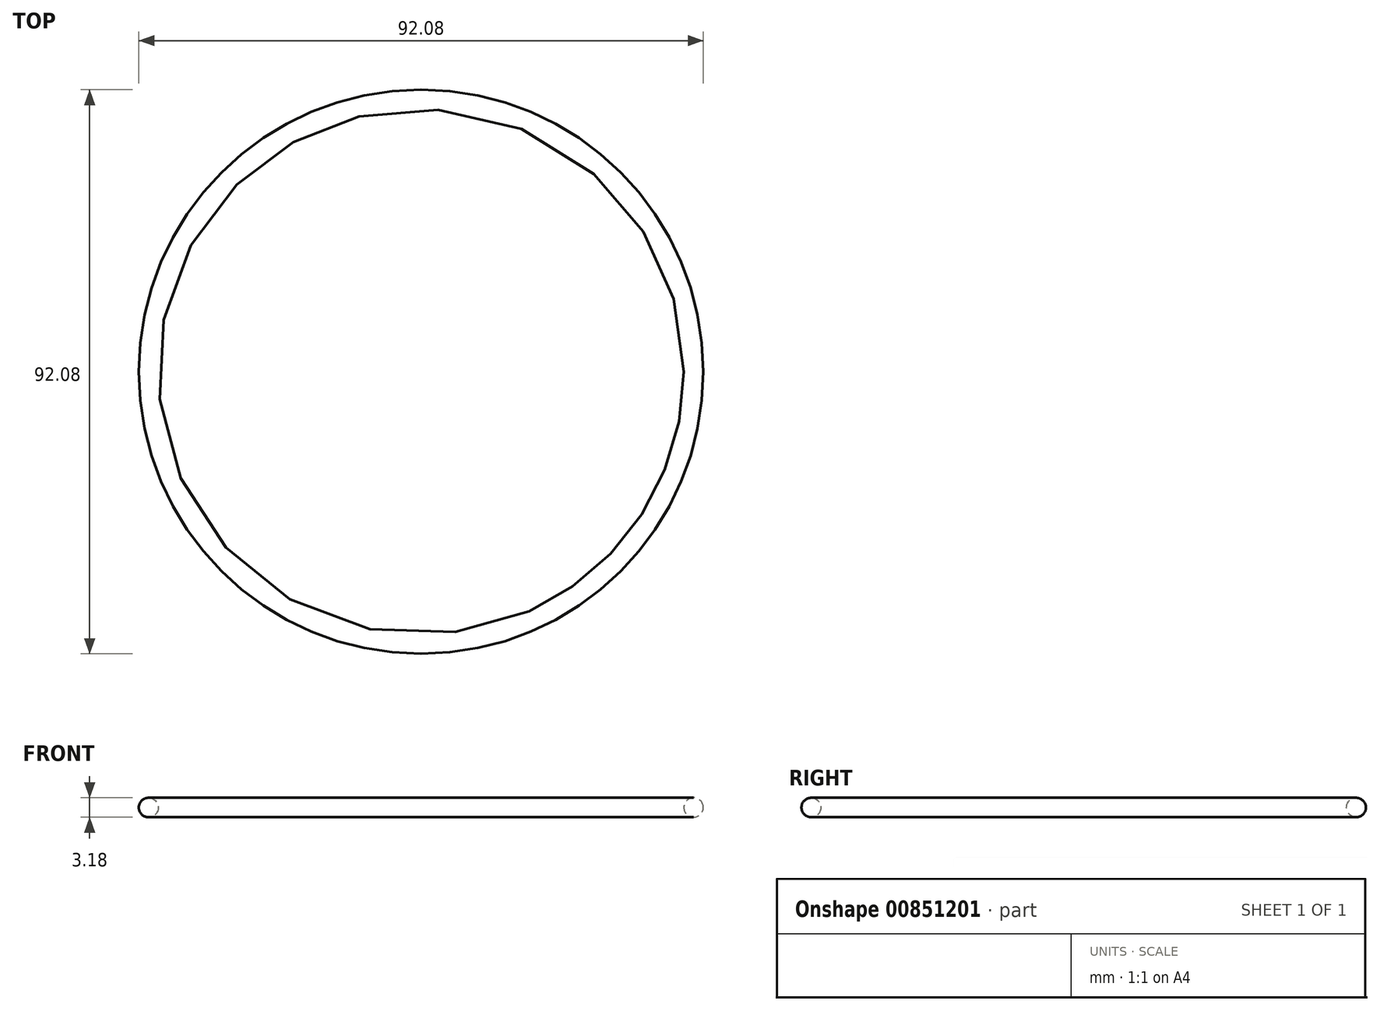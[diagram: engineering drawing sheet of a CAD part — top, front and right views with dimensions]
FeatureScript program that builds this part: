
annotation { "Feature Type Name" : "Feature", "Feature Type Description" : "" }
export const myFeature = defineFeature(function(context is Context, id is Id, definition is map)
    precondition{}
    {
        {
            var Q0;
            Q0=qCreatedBy(makeId("Front.planeOp"),FACE);
            var sketch = newSketch(context, id + "F0", { "sketchPlane" : qUnion([Q0])});
            skCircle(sketch, "E0", {"center": v(44.45, 0) * mm, "radius": 1.59 * mm});
            skLineSegment(sketch, "E1", {"start": v(0, 25.48) * mm, "end": v(0, -38.22) * mm, "construction": true});
            skSolve(sketch);
        }
        {
            var Q0;
            Q0=makeQuery(id+"F0.imprint","IMPRINT",FACE,{"disambiguationData":[TD([[makeQuery(id+"F0.imprint","IMPRINT",EDGE,{"derivedFrom":sQuery(id+"F0.wireOp",EDGE,"E0")}),1.0]])]});
            var Q1;
            Q1=sQuery(id+"F0.wireOp",EDGE,"E1");
            revolve(context, id + "F1", {"surfaceOperationType" : NewSurfaceOperationType.NEW, "entities" : qUnion([Q0]), "axis" : qUnion([Q1]), "revolveType" : RevolveType.FULL});
        }
    });
